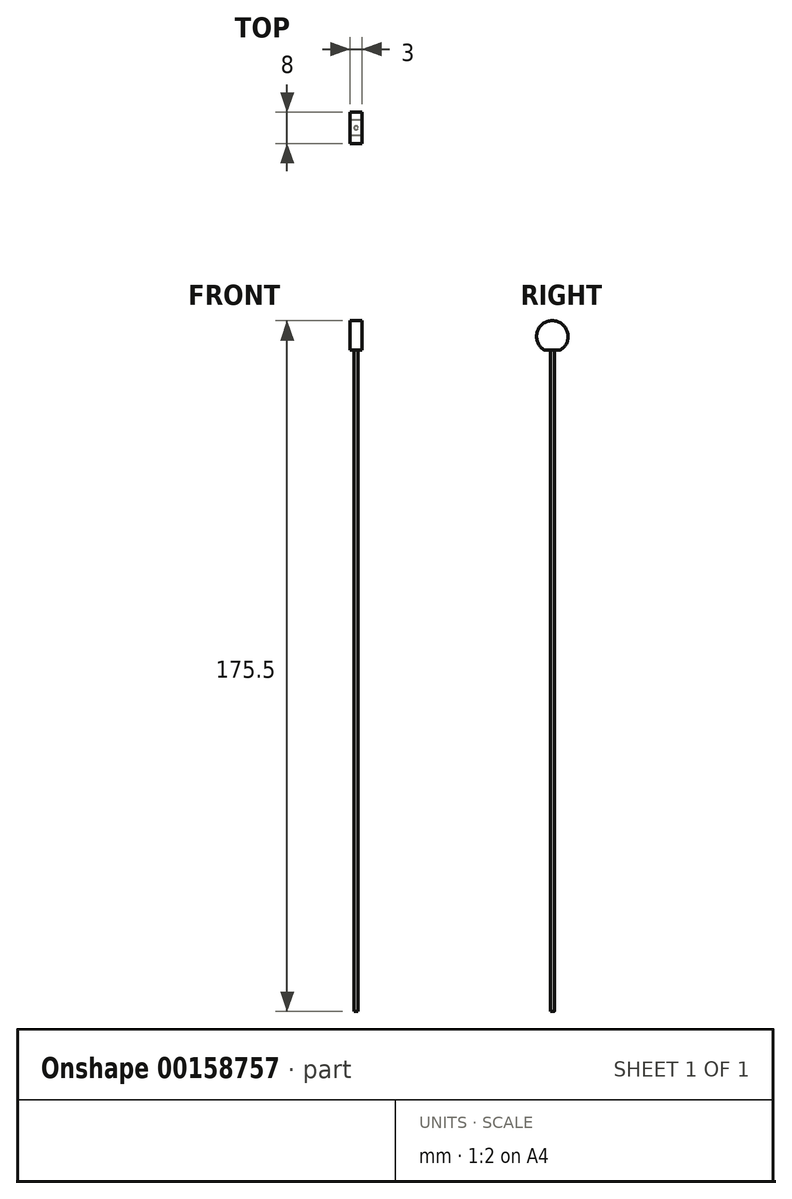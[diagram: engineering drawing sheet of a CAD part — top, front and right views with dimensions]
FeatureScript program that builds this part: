
annotation { "Feature Type Name" : "Feature", "Feature Type Description" : "" }
export const myFeature = defineFeature(function(context is Context, id is Id, definition is map)
    precondition{}
    {
        {
            var Q0;
            Q0=qCreatedBy(makeId("Top.planeOp"),FACE);
            var sketch = newSketch(context, id + "F0", { "sketchPlane" : qUnion([Q0])});
            skCircle(sketch, "E0", {"center": v(0, 0) * mm, "radius": 0.5 * mm});
            skSolve(sketch);
        }
        {
            var Q0;
            Q0=makeQuery(id+"F0.imprint","IMPRINT",FACE,{"disambiguationData":[TD([[makeQuery(id+"F0.imprint","IMPRINT",EDGE,{"derivedFrom":sQuery(id+"F0.wireOp",EDGE,"E0")}),1.0]])]});
            extrude(context, id + "F1", {"entities" : qUnion([Q0]), "depth" : 168 * mm, "symmetric" : true});
        }
        {
            var Q0;
            Q0=qCreatedBy(makeId("Right.planeOp"),FACE);
            var sketch = newSketch(context, id + "F2", { "sketchPlane" : qUnion([Q0])});
            skCircle(sketch, "E1", {"center": v(0, 87.5) * mm, "radius": 4 * mm});
            skLineSegment(sketch, "E2", {"start": v(-1.94, 84) * mm, "end": v(1.94, 84) * mm});
            skSolve(sketch);
        }
        {
            var Q0;
            {var subQ0=sQuery(id+"F2.wireOp",EDGE,"E2");Q0=makeQuery(id+"F2.imprint","IMPRINT",FACE,{"disambiguationData":[TD([[makeQuery(id+"F2.imprint","IMPRINT",EDGE,{"derivedFrom":subQ0}),1.0]])]});}
            extrude(context, id + "F3", {"entities" : qUnion([Q0]), "operationType" : NewBodyOperationType.ADD, "depth" : 3 * mm, "symmetric" : true});
        }
    });
